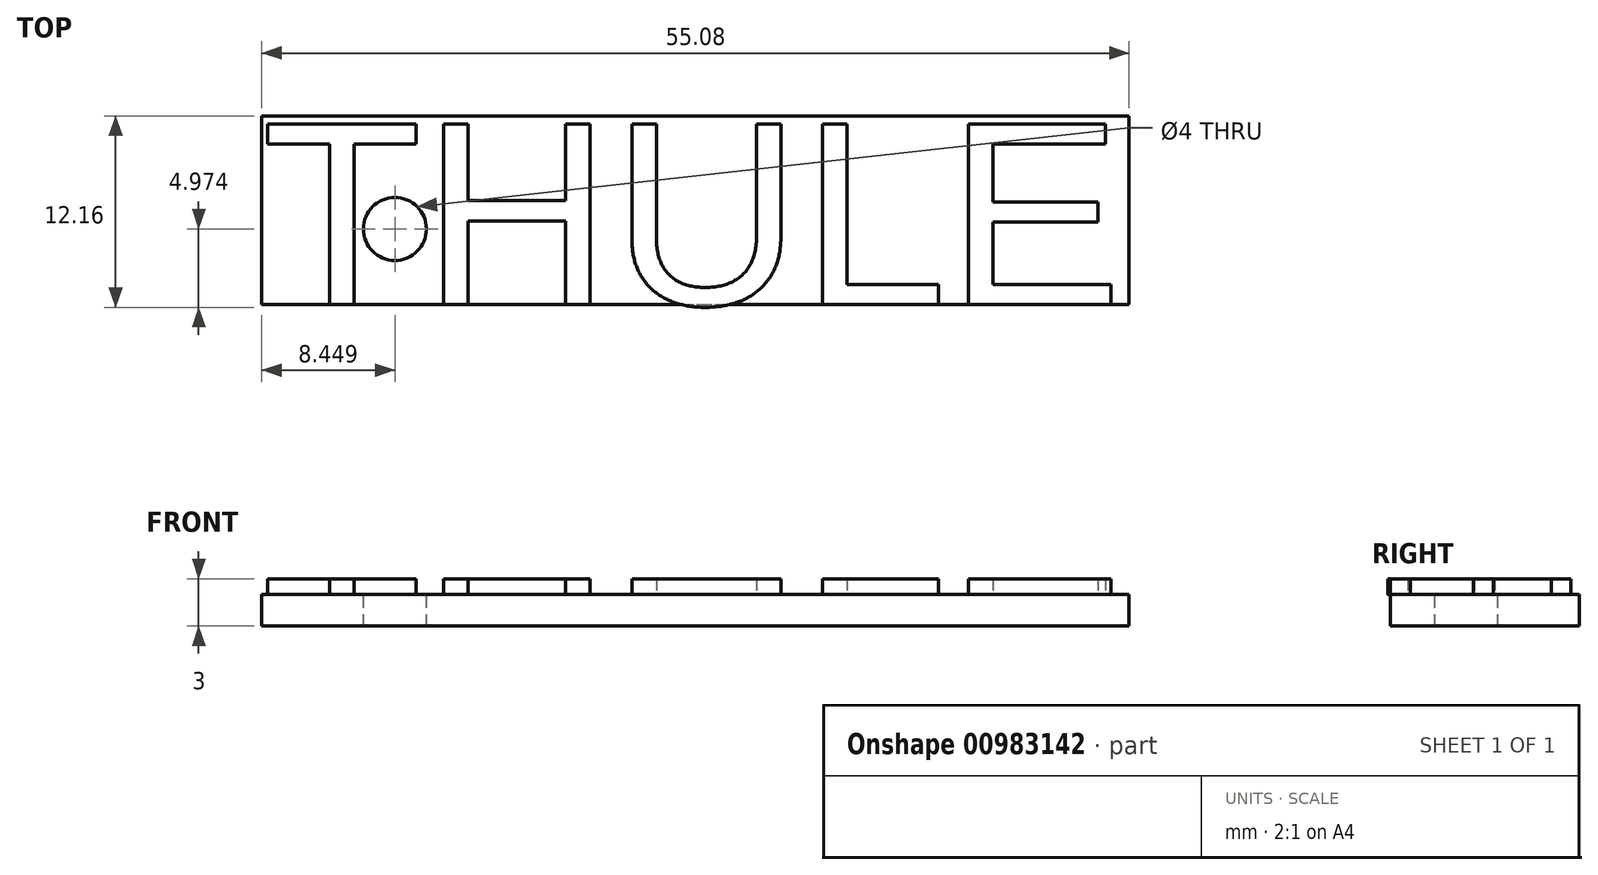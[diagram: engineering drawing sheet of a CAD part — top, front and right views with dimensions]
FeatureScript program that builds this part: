
annotation { "Feature Type Name" : "Feature", "Feature Type Description" : "" }
export const myFeature = defineFeature(function(context is Context, id is Id, definition is map)
    precondition{}
    {
        {
            var Q0;
            Q0=qCreatedBy(makeId("Top.planeOp"),FACE);
            var sketch = newSketch(context, id + "F0", { "sketchPlane" : qUnion([Q0])});
            skText(sketch, "E0", { "text": "THULE", "fontName": "Arimo-Regular.ttf"});
            const initialGuessF0  = {"E0": [-0.04097, 0, 1, 0, 0.012]};
            skSetInitialGuess(sketch, initialGuessF0);
            skSolve(sketch);
        }
        {
            var Q0;
            Q0=qCreatedBy(makeId("Top.planeOp"),FACE);
            var sketch = newSketch(context, id + "F1", { "sketchPlane" : qUnion([Q0])});
            skLineSegment(sketch, "E1.0", {"start": v(-40.97, 12) * mm, "end": v(14.1, 12) * mm});
            skLineSegment(sketch, "E2.0", {"start": v(-40.97, 0) * mm, "end": v(-40.97, 12) * mm});
            skLineSegment(sketch, "E3.0", {"start": v(-40.97, 0) * mm, "end": v(14.1, 0) * mm});
            skLineSegment(sketch, "E4.0", {"start": v(14.1, 0) * mm, "end": v(14.1, 12) * mm});
            skSolve(sketch);
        }
        {
            var Q0;
            Q0 = qSketchRegion(id + "F0", true);
            extrude(context, id + "F2", {"entities" : qUnion([Q0]), "depth" : 1 * mm, "offsetDistance" : 25 * mm});
        }
        {
            var Q0;
            Q0 = qSketchRegion(id + "F1", true);
            extrude(context, id + "F3", {"entities" : qUnion([Q0]), "oppositeDirection" : true, "depth" : 2 * mm, "offsetDistance" : 25 * mm});
        }
        {
            var Q0;
            Q0=makeQuery(id+"F3.opExtrude","CAP_FACE",FACE,{"disambiguationData":[OSD([sQuery(id+"F1.wireOp",EDGE,"E1.0"),sQuery(id+"F1.wireOp",EDGE,"E2.0"),sQuery(id+"F1.wireOp",EDGE,"E3.0"),sQuery(id+"F1.wireOp",EDGE,"E4.0")])],"isStart":true});
            var sketch = newSketch(context, id + "F4", { "sketchPlane" : qUnion([Q0])});
            skCircle(sketch, "E5", {"center": v(-32.52, 4.81) * mm, "radius": 2 * mm});
            skSolve(sketch);
        }
        {
            var Q0;
            Q0 = qSketchRegion(id + "F4", true);
            extrude(context, id + "F5", {"entities" : qUnion([Q0]), "operationType" : NewBodyOperationType.REMOVE, "endBound" : BoundingType.THROUGH_ALL, "oppositeDirection" : true, "depth" : 25 * mm, "offsetDistance" : 25 * mm});
        }
    });
